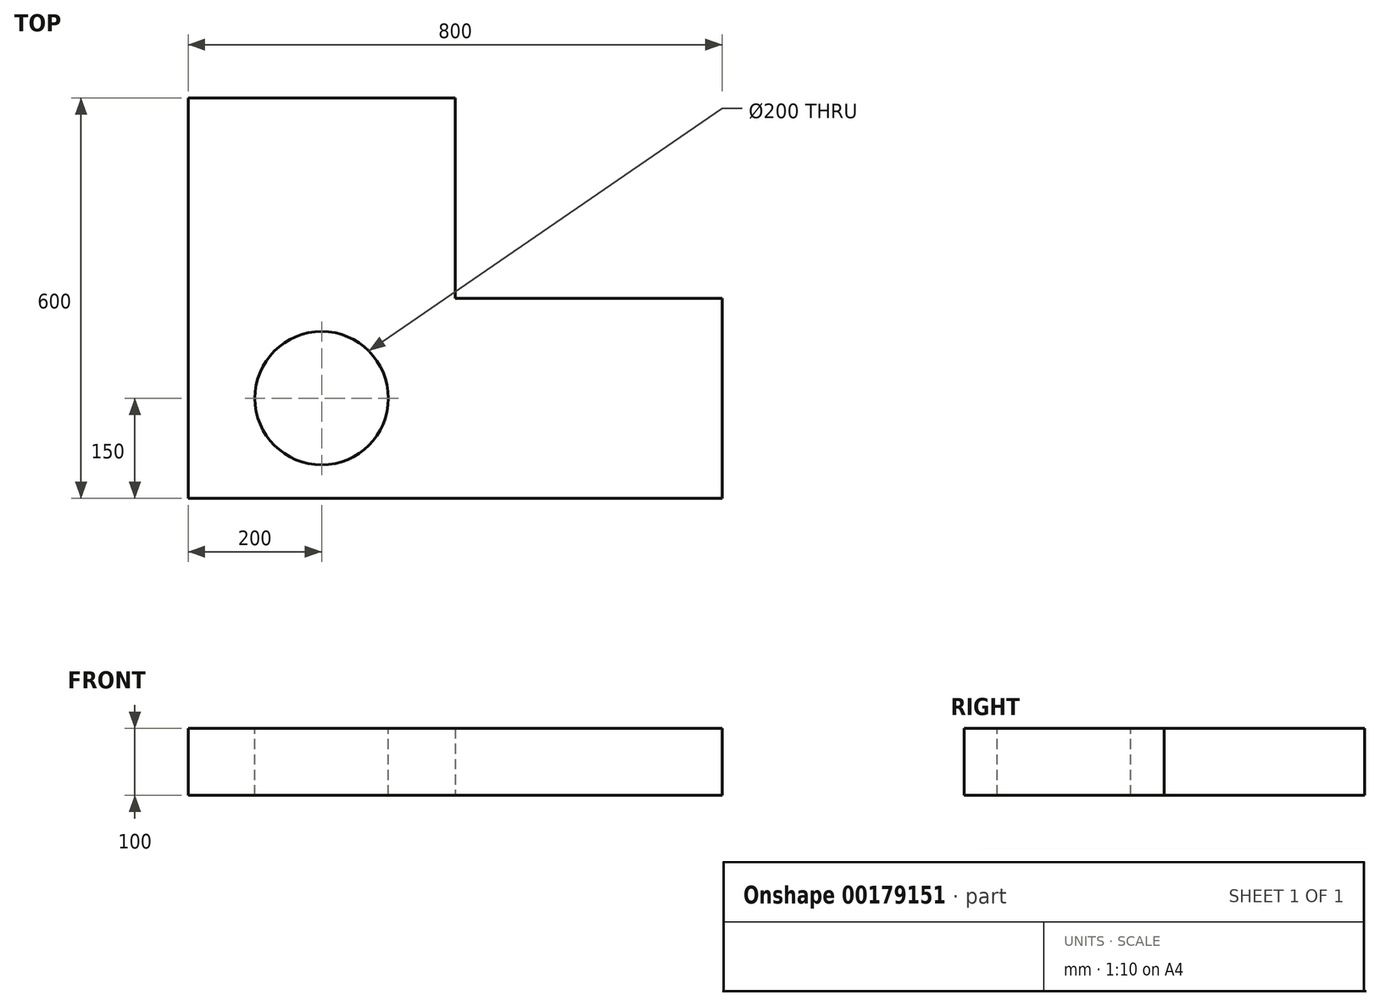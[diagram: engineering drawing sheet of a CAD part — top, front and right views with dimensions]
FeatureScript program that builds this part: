
annotation { "Feature Type Name" : "Feature", "Feature Type Description" : "" }
export const myFeature = defineFeature(function(context is Context, id is Id, definition is map)
    precondition{}
    {
        {
            var Q0;
            Q0=qCreatedBy(makeId("Top.planeOp"),FACE);
            var sketch = newSketch(context, id + "F0", { "sketchPlane" : qUnion([Q0])});
            skLineSegment(sketch, "E0", {"start": v(0, 0) * mm, "end": v(800, 0) * mm});
            skLineSegment(sketch, "E1", {"start": v(800, 0) * mm, "end": v(800, 300) * mm});
            skLineSegment(sketch, "E2", {"start": v(800, 300) * mm, "end": v(400, 300) * mm});
            skLineSegment(sketch, "E3", {"start": v(400, 300) * mm, "end": v(400, 600) * mm});
            skLineSegment(sketch, "E4", {"start": v(400, 600) * mm, "end": v(0, 600) * mm});
            skLineSegment(sketch, "E5", {"start": v(0, 600) * mm, "end": v(0, 0) * mm});
            skSolve(sketch);
        }
        {
            var Q0;
            Q0=makeQuery(id+"F0.imprint","IMPRINT",FACE,{"disambiguationData":[TD([[makeQuery(id+"F0.imprint","IMPRINT",EDGE,{"derivedFrom":sQuery(id+"F0.wireOp",EDGE,"E0")}),1.0]])]});
            extrude(context, id + "F1", {"entities" : qUnion([Q0]), "depth" : 100 * mm});
        }
        {
            var Q0;
            Q0=makeQuery(id+"F1.opExtrude","CAP_FACE",FACE,{"disambiguationData":[OSD([sQuery(id+"F0.wireOp",EDGE,"E0"),sQuery(id+"F0.wireOp",EDGE,"E1"),sQuery(id+"F0.wireOp",EDGE,"E2"),sQuery(id+"F0.wireOp",EDGE,"E3"),sQuery(id+"F0.wireOp",EDGE,"E4"),sQuery(id+"F0.wireOp",EDGE,"E5")])],"isStart":false});
            var sketch = newSketch(context, id + "F2", { "sketchPlane" : qUnion([Q0])});
            skLineSegment(sketch, "E6", {"start": v(200, 600) * mm, "end": v(200, 0) * mm, "construction": true});
            skLineSegment(sketch, "E7", {"start": v(800, 150) * mm, "end": v(0, 150) * mm, "construction": true});
            skCircle(sketch, "E8", {"center": v(200, 150) * mm, "radius": 100 * mm});
            skSolve(sketch);
        }
        {
            var Q0;
            Q0=makeQuery(id+"F2.imprint","IMPRINT",FACE,{"disambiguationData":[TD([[makeQuery(id+"F2.imprint","IMPRINT",EDGE,{"derivedFrom":sQuery(id+"F2.wireOp",EDGE,"E8")}),1.0]])]});
            extrude(context, id + "F3", {"entities" : qUnion([Q0]), "operationType" : NewBodyOperationType.REMOVE, "oppositeDirection" : true, "depth" : 100 * mm});
        }
    });
